# Revit family: 7265 Велопарковка VELO-5 Хоббика
name_source: partatom
category: Антураж
revit_build: Autodesk Revit 2018 (Build: 20180423_1000(x64)
units: mm (PartAtom-declared; Revit-internal decimal feet)

## family parameters
Всегда вертикально = Да
Источник визуального образа = Геометрия семейства
На основе рабочей плоскости = Нет
Общий = Нет
При загрузке вырезать с полостями = Нет
Точка расчета площади = Нет

## types (6) — shared parameters
URL = https://hobbyka.ru
Артикул товара = Арт. 7265
Высота = 1115 мм
Группа модели = Велопарковки
Изготовитель = ООО «Хоббика»
Изображение типоразмера = Велопарковка VELO-5 Арт 7265.jpg
Цвет каркаса = Сталь
Ширина = 1138 мм

## per-type parameters (varying)
| type | 11 мест | 4 места | 5 мест | 5 мест (нерж.сталь) | 7 мест | 8 мест | Длина | Кол-во средних мест | Материал изделия | Описание |
| 4 места | Нет | Да | Нет | Нет | Нет | Нет | 1426 мм | 2 | Сталь | Велопарковка VELO-5. Версия на 4 места |
| 5 мест | Нет | Нет | Да | Нет | Нет | Нет | 1844 мм | 3 | Сталь | Велопарковка VELO-5. Версия на 5 мест |
| 5 мест (нерж.сталь) | Нет | Нет | Нет | Да | Нет | Нет | 1844 мм | 3 | Нержавеющая сталь | Велопарковка VELO-5. Версия на 5 мест из нержавеющей стали |
| 7 мест | Нет | Нет | Нет | Нет | Да | Нет | 2696 мм | 5 | Сталь | Велопарковка VELO-5. Версия на 7 мест |
| 8 мест | Нет | Нет | Нет | Нет | Нет | Да | 3141 мм | 6 | Сталь | Велопарковка VELO-5. Версия на 8 мест |
| 11 мест | Да | Нет | Нет | Нет | Нет | Нет | 4352 мм | 9 | Сталь | Велопарковка VELO-5. Версия на 11 мест |
